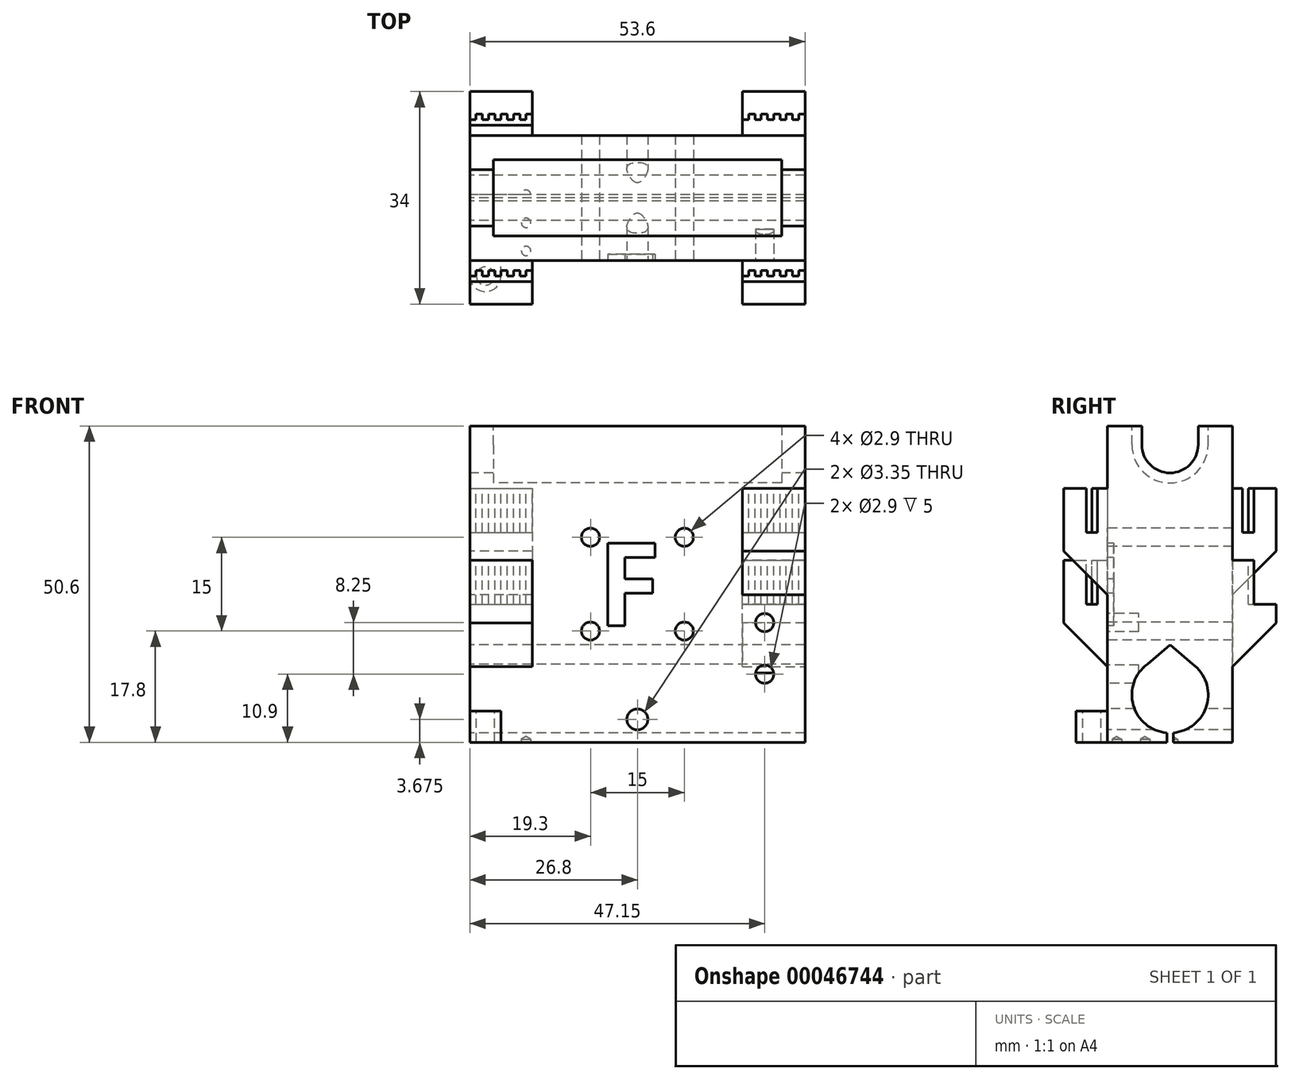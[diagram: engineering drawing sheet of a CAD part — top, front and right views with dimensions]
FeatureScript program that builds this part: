
annotation { "Feature Type Name" : "Feature", "Feature Type Description" : "" }
export const myFeature = defineFeature(function(context is Context, id is Id, definition is map)
    precondition{}
    {
        {
            assignVariable(context, id + "F0", {"name" : "LM8LUU", "anyValue" : 1.8});
        }
        {
            var Q0;
            Q0=qCreatedBy(makeId("Top.planeOp"),FACE);
            var sketch = newSketch(context, id + "F1", { "sketchPlane" : qUnion([Q0])});
            skLineSegment(sketch, "E0.bottom", {"start": v(0, 0) * mm, "end": v(53.6, 0) * mm});
            skLineSegment(sketch, "E0.top", {"start": v(0, 20) * mm, "end": v(53.6, 20) * mm});
            skLineSegment(sketch, "E0.left", {"start": v(0, 0) * mm, "end": v(0, 20) * mm});
            skLineSegment(sketch, "E0.right", {"start": v(53.6, 0) * mm, "end": v(53.6, 20) * mm});
            skSolve(sketch);
        }
        {
            var Q0;
            Q0=qSketchRegion(id+"F1",true);
            extrude(context, id + "F2", {"entities" : qUnion([Q0]), "depth" : 50.6 * mm});
        }
        {
            var Q0;
            Q0=makeQuery(id+"F2.opExtrude","SWEPT_FACE",FACE,{"disambiguationData":[OSD([sQuery(id+"F1.wireOp",EDGE,"E0.left")])]});
            var sketch = newSketch(context, id + "F3", { "sketchPlane" : qUnion([Q0])});
            skCircle(sketch, "E1", {"center": v(-10, 7.6) * mm, "radius": 6.1 * mm});
            skCircle(sketch, "E2", {"center": v(-10, 47.6) * mm, "radius": 4.5 * mm});
            skLineSegment(sketch, "E3", {"start": v(-20, 47.6) * mm, "end": v(0, 47.6) * mm, "construction": true});
            skLineSegment(sketch, "E4", {"start": v(-14.5, 50.6) * mm, "end": v(-14.5, 47.6) * mm});
            skLineSegment(sketch, "E5", {"start": v(-5.5, 50.6) * mm, "end": v(-5.5, 47.6) * mm});
            skLineSegment(sketch, "E6", {"start": v(-20, 7.6) * mm, "end": v(0, 7.6) * mm, "construction": true});
            skLineSegment(sketch, "E7", {"start": v(-10, 7.6) * mm, "end": v(-10, 0) * mm, "construction": true});
            skLineSegment(sketch, "E8", {"start": v(-10, 0) * mm, "end": v(-10.5, 0) * mm});
            skLineSegment(sketch, "E9", {"start": v(-10.5, 0) * mm, "end": v(-10.5, 1.52) * mm});
            skLineSegment(sketch, "E10", {"start": v(-10.5, 1.52) * mm, "end": v(-9.5, 1.52) * mm});
            skLineSegment(sketch, "E11", {"start": v(-9.5, 1.52) * mm, "end": v(-9.5, 0) * mm});
            skLineSegment(sketch, "E12", {"start": v(-9.5, 0) * mm, "end": v(-10, 0) * mm});
            skLineSegment(sketch, "E13", {"start": v(-10, 13.7) * mm, "end": v(-10, 15.6) * mm});
            skLineSegment(sketch, "E14", {"start": v(-10, 15.6) * mm, "end": v(-6.39, 12.51) * mm});
            skLineSegment(sketch, "E15", {"start": v(-10, 15.6) * mm, "end": v(-13.61, 12.51) * mm});
            skCircle(sketch, "E16", {"center": v(-10, 47.6) * mm, "radius": 6.1 * mm});
            skLineSegment(sketch, "E17", {"start": v(-3.9, 47.6) * mm, "end": v(-3.9, 50.6) * mm});
            skLineSegment(sketch, "E18", {"start": v(-16.1, 47.6) * mm, "end": v(-16.1, 50.6) * mm});
            skSolve(sketch);
        }
        {
            var Q0;
            {var subQ0=sQuery(id+"F3.wireOp",EDGE,"E14");var subQ1=sQuery(id+"F3.wireOp",EDGE,"E1");var subQ3=makeQuery(id+"F3.imprint","INTERSECT",VERTEX,{"disambiguationData":[OD(0.0)],"derivedFrom":[subQ1,subQ0]});Q0=makeQuery(id+"F3.imprint","IMPRINT",FACE,{"disambiguationData":[TD([[makeQuery(id+"F3.imprint","IMPRINT",EDGE,{"disambiguationData":[TD([[subQ3,-1.0]])],"derivedFrom":subQ1}),1.0]])]});}
            var Q1;
            {var subQ0=sQuery(id+"F3.wireOp",EDGE,"E15");var subQ1=sQuery(id+"F3.wireOp",EDGE,"E1");var subQ3=makeQuery(id+"F3.imprint","INTERSECT",VERTEX,{"disambiguationData":[OD(0.0)],"derivedFrom":[subQ1,subQ0]});Q1=makeQuery(id+"F3.imprint","IMPRINT",FACE,{"disambiguationData":[TD([[makeQuery(id+"F3.imprint","IMPRINT",EDGE,{"disambiguationData":[TD([[subQ3,1.0]])],"derivedFrom":subQ1}),1.0]])]});}
            var Q2;
            Q2=makeQuery(id+"F3.imprint","IMPRINT",FACE,{"disambiguationData":[TD([[makeQuery(id+"F3.imprint","IMPRINT",EDGE,{"derivedFrom":sQuery(id+"F3.wireOp",EDGE,"E8")}),-1.0]])]});
            var Q3;
            {var subQ0=sQuery(id+"F3.wireOp",EDGE,"E10");Q3=makeQuery(id+"F3.imprint","IMPRINT",FACE,{"disambiguationData":[TD([[makeQuery(id+"F3.imprint","IMPRINT",EDGE,{"derivedFrom":subQ0}),-1.0]])]});}
            var Q4;
            {var subQ3=sQuery(id+"F3.wireOp",EDGE,"E13");Q4=makeQuery(id+"F3.imprint","IMPRINT",FACE,{"disambiguationData":[TD([[makeQuery(id+"F3.imprint","IMPRINT",EDGE,{"derivedFrom":subQ3}),-1.0]])]});}
            var Q5;
            {var subQ3=sQuery(id+"F3.wireOp",EDGE,"E13");Q5=makeQuery(id+"F3.imprint","IMPRINT",FACE,{"disambiguationData":[TD([[makeQuery(id+"F3.imprint","IMPRINT",EDGE,{"derivedFrom":subQ3}),1.0]])]});}
            var Q6;
            {var subQ7=sQuery(id+"F3.wireOp",EDGE,"E10");Q6=makeQuery(id+"F3.imprint","IMPRINT",FACE,{"disambiguationData":[TD([[makeQuery(id+"F3.imprint","IMPRINT",EDGE,{"derivedFrom":subQ7}),1.0]])]});}
            var Q7;
            {var subQ3=sQuery(id+"F3.wireOp",EDGE,"E5");Q7=makeQuery(id+"F3.imprint","IMPRINT",FACE,{"disambiguationData":[TD([[makeQuery(id+"F3.imprint","IMPRINT",EDGE,{"derivedFrom":subQ3}),-1.0]])]});}
            var Q8;
            {var subQ0=sQuery(id+"F3.wireOp",EDGE,"E4");Q8=makeQuery(id+"F3.imprint","IMPRINT",FACE,{"disambiguationData":[TD([[makeQuery(id+"F3.imprint","IMPRINT",EDGE,{"derivedFrom":subQ0}),1.0]])]});}
            var Q9;
            {var subQ0=sQuery(id+"F3.wireOp",EDGE,"E4");Q9=makeQuery(id+"F3.imprint","IMPRINT",FACE,{"disambiguationData":[TD([[makeQuery(id+"F3.imprint","IMPRINT",EDGE,{"derivedFrom":subQ0}),1.0]])]});}
            var Q10;
            {var subQ3=sQuery(id+"F3.wireOp",EDGE,"E5");Q10=makeQuery(id+"F3.imprint","IMPRINT",FACE,{"disambiguationData":[TD([[makeQuery(id+"F3.imprint","IMPRINT",EDGE,{"derivedFrom":subQ3}),-1.0]])]});}
            var Q11;
            {var subQ1=sQuery(id+"F3.wireOp",EDGE,"E2");var subQ4=makeQuery(id+"F3.imprint","INTERSECT",VERTEX,{"derivedFrom":[subQ1,sQuery(id+"F3.wireOp",EDGE,"E5")]});Q11=makeQuery(id+"F3.imprint","IMPRINT",FACE,{"disambiguationData":[TD([[makeQuery(id+"F3.imprint","IMPRINT",EDGE,{"disambiguationData":[TD([[subQ4,-1.0]])],"derivedFrom":subQ1}),1.0]])]});}
            extrude(context, id + "F4", {"entities" : qUnion([Q0, Q1, Q2, Q3, Q4, Q5, Q6, Q7, Q8, Q9, Q10, Q11]), "operationType" : NewBodyOperationType.REMOVE, "endBound" : BoundingType.THROUGH_ALL, "oppositeDirection" : true, "depth" : 25 * mm});
        }
        {
            var Q0;
            {var subQ3=sQuery(id+"F3.wireOp",EDGE,"E4");Q0=makeQuery(id+"F3.imprint","IMPRINT",FACE,{"disambiguationData":[TD([[makeQuery(id+"F3.imprint","IMPRINT",EDGE,{"derivedFrom":subQ3}),-1.0]])]});}
            var Q1;
            {var subQ3=sQuery(id+"F3.wireOp",EDGE,"E18");Q1=makeQuery(id+"F3.imprint","IMPRINT",FACE,{"disambiguationData":[TD([[makeQuery(id+"F3.imprint","IMPRINT",EDGE,{"derivedFrom":subQ3}),-1.0]])]});}
            var Q2;
            {var subQ3=sQuery(id+"F3.wireOp",EDGE,"E17");Q2=makeQuery(id+"F3.imprint","IMPRINT",FACE,{"disambiguationData":[TD([[makeQuery(id+"F3.imprint","IMPRINT",EDGE,{"derivedFrom":subQ3}),1.0]])]});}
            extrude(context, id + "F5", {"entities" : qUnion([Q0, Q1, Q2]), "operationType" : NewBodyOperationType.REMOVE, "oppositeDirection" : true, "depth" : (46.25 + getVariable(context, 'LM8LUU') * 2) * mm});
        }
        {
            var Q0;
            {var subQ3=sQuery(id+"F3.wireOp",EDGE,"E4");Q0=makeQuery(id+"F3.imprint","IMPRINT",FACE,{"disambiguationData":[TD([[makeQuery(id+"F3.imprint","IMPRINT",EDGE,{"derivedFrom":subQ3}),-1.0]])]});}
            var Q1;
            {var subQ3=sQuery(id+"F3.wireOp",EDGE,"E18");Q1=makeQuery(id+"F3.imprint","IMPRINT",FACE,{"disambiguationData":[TD([[makeQuery(id+"F3.imprint","IMPRINT",EDGE,{"derivedFrom":subQ3}),-1.0]])]});}
            var Q2;
            {var subQ3=sQuery(id+"F3.wireOp",EDGE,"E17");Q2=makeQuery(id+"F3.imprint","IMPRINT",FACE,{"disambiguationData":[TD([[makeQuery(id+"F3.imprint","IMPRINT",EDGE,{"derivedFrom":subQ3}),1.0]])]});}
            extrude(context, id + "F6", {"entities" : qUnion([Q0, Q1, Q2]), "operationType" : NewBodyOperationType.ADD, "oppositeDirection" : true, "depth" : (26.75 - getVariable(context, 'LM8LUU')) * mm});
        }
        {
            var Q0;
            {var subQ3=sQuery(id+"F3.wireOp",EDGE,"E4");Q0=makeQuery(id+"F3.imprint","IMPRINT",FACE,{"disambiguationData":[TD([[makeQuery(id+"F3.imprint","IMPRINT",EDGE,{"derivedFrom":subQ3}),-1.0]])]});}
            var Q1;
            {var subQ3=sQuery(id+"F3.wireOp",EDGE,"E18");Q1=makeQuery(id+"F3.imprint","IMPRINT",FACE,{"disambiguationData":[TD([[makeQuery(id+"F3.imprint","IMPRINT",EDGE,{"derivedFrom":subQ3}),-1.0]])]});}
            var Q2;
            {var subQ3=sQuery(id+"F3.wireOp",EDGE,"E17");Q2=makeQuery(id+"F3.imprint","IMPRINT",FACE,{"disambiguationData":[TD([[makeQuery(id+"F3.imprint","IMPRINT",EDGE,{"derivedFrom":subQ3}),1.0]])]});}
            extrude(context, id + "F7", {"entities" : qUnion([Q0, Q1, Q2]), "operationType" : NewBodyOperationType.REMOVE, "oppositeDirection" : true, "depth" : (23.25 + getVariable(context, 'LM8LUU')) * mm});
        }
        {
            var Q0;
            {var subQ3=sQuery(id+"F3.wireOp",EDGE,"E4");Q0=makeQuery(id+"F3.imprint","IMPRINT",FACE,{"disambiguationData":[TD([[makeQuery(id+"F3.imprint","IMPRINT",EDGE,{"derivedFrom":subQ3}),-1.0]])]});}
            var Q1;
            {var subQ3=sQuery(id+"F3.wireOp",EDGE,"E18");Q1=makeQuery(id+"F3.imprint","IMPRINT",FACE,{"disambiguationData":[TD([[makeQuery(id+"F3.imprint","IMPRINT",EDGE,{"derivedFrom":subQ3}),-1.0]])]});}
            var Q2;
            {var subQ3=sQuery(id+"F3.wireOp",EDGE,"E17");Q2=makeQuery(id+"F3.imprint","IMPRINT",FACE,{"disambiguationData":[TD([[makeQuery(id+"F3.imprint","IMPRINT",EDGE,{"derivedFrom":subQ3}),1.0]])]});}
            extrude(context, id + "F8", {"entities" : qUnion([Q0, Q1, Q2]), "operationType" : NewBodyOperationType.ADD, "oppositeDirection" : true, "depth" : 3.75 * mm});
        }
        {
            var Q0;
            Q0=makeQuery(id+"F2.opExtrude","SWEPT_FACE",FACE,{"disambiguationData":[OSD([sQuery(id+"F1.wireOp",EDGE,"E0.bottom")])]});
            var sketch = newSketch(context, id + "F9", { "sketchPlane" : qUnion([Q0])});
            skLineSegment(sketch, "E19.bottom", {"start": v(0, 29.1) * mm, "end": v(10, 29.1) * mm});
            skLineSegment(sketch, "E19.top", {"start": v(0, 9.1) * mm, "end": v(10, 9.1) * mm});
            skLineSegment(sketch, "E19.left", {"start": v(0, 29.1) * mm, "end": v(0, 9.1) * mm});
            skLineSegment(sketch, "E19.right", {"start": v(10, 29.1) * mm, "end": v(10, 9.1) * mm});
            skLineSegment(sketch, "E20.bottom", {"start": v(53.6, 40.6) * mm, "end": v(43.6, 40.6) * mm});
            skLineSegment(sketch, "E20.top", {"start": v(53.6, 20.6) * mm, "end": v(43.6, 20.6) * mm});
            skLineSegment(sketch, "E20.left", {"start": v(53.6, 40.6) * mm, "end": v(53.6, 20.6) * mm});
            skLineSegment(sketch, "E20.right", {"start": v(43.6, 40.6) * mm, "end": v(43.6, 20.6) * mm});
            skPoint(sketch, "E21", {"position": v(0, 47.6) * mm});
            skPoint(sketch, "E22", {"position": v(0, 8.6) * mm});
            skSolve(sketch);
        }
        {
            var Q0;
            Q0=qSketchRegion(id+"F9",true);
            extrude(context, id + "F10", {"entities" : qUnion([Q0]), "operationType" : NewBodyOperationType.ADD, "depth" : 7 * mm});
        }
        {
            var Q0;
            Q0=makeQuery(id+"F10.opExtrude","CAP_EDGE",EDGE,{"disambiguationData":[OSD([sQuery(id+"F9.wireOp",EDGE,"E19.top")])],"isStart":false});
            var Q1;
            Q1=makeQuery(id+"F10.opExtrude","CAP_EDGE",EDGE,{"disambiguationData":[OSD([sQuery(id+"F9.wireOp",EDGE,"E20.top")])],"isStart":false});
            chamfer(context, id + "F11", {"entities" : qUnion([Q0, Q1]), "width" : 10 * mm, "tangentPropagation" : true});
        }
        {
            var Q0;
            Q0=makeQuery(id+"F10.opExtrude","SWEPT_FACE",FACE,{"disambiguationData":[OSD([sQuery(id+"F9.wireOp",EDGE,"E19.bottom")])]});
            var sketch = newSketch(context, id + "F12", { "sketchPlane" : qUnion([Q0])});
            skLineSegment(sketch, "E23", {"start": v(-935.9, 0) * mm, "end": v(-935.88, -4.54) * mm});
            skLineSegment(sketch, "E24.left", {"start": v(0, -3.4) * mm, "end": v(0, -1.6) * mm});
            skLineSegment(sketch, "E25", {"start": v(6, -2.5) * mm, "end": v(7, -2.5) * mm});
            skLineSegment(sketch, "E26", {"start": v(4, -2.5) * mm, "end": v(5, -2.5) * mm});
            skLineSegment(sketch, "E27", {"start": v(0, -2.5) * mm, "end": v(1, -2.5) * mm});
            skLineSegment(sketch, "E28", {"start": v(7, -1.6) * mm, "end": v(8, -1.6) * mm});
            skLineSegment(sketch, "E29", {"start": v(2, -2.5) * mm, "end": v(3, -2.5) * mm});
            skLineSegment(sketch, "E30", {"start": v(3, -1.6) * mm, "end": v(4, -1.6) * mm});
            skLineSegment(sketch, "E31", {"start": v(8, -2.5) * mm, "end": v(9, -2.5) * mm});
            skLineSegment(sketch, "E32", {"start": v(8, -1.6) * mm, "end": v(8, -2.5) * mm});
            skLineSegment(sketch, "E33", {"start": v(9, -2.5) * mm, "end": v(9, -1.6) * mm});
            skLineSegment(sketch, "E34", {"start": v(10, -1.6) * mm, "end": v(10, -2.5) * mm});
            skLineSegment(sketch, "E35", {"start": v(6, -1.6) * mm, "end": v(6, -2.5) * mm});
            skLineSegment(sketch, "E36", {"start": v(2, -1.6) * mm, "end": v(2, -2.5) * mm});
            skLineSegment(sketch, "E37", {"start": v(1, -1.6) * mm, "end": v(2, -1.6) * mm});
            skLineSegment(sketch, "E38", {"start": v(1, -2.5) * mm, "end": v(1, -1.6) * mm});
            skLineSegment(sketch, "E39", {"start": v(9, -1.6) * mm, "end": v(10, -1.6) * mm});
            skLineSegment(sketch, "E40", {"start": v(5, -1.6) * mm, "end": v(6, -1.6) * mm});
            skLineSegment(sketch, "E41", {"start": v(5, -2.5) * mm, "end": v(5, -1.6) * mm});
            skLineSegment(sketch, "E42", {"start": v(3, -2.5) * mm, "end": v(3, -1.6) * mm});
            skLineSegment(sketch, "E43", {"start": v(4, -1.6) * mm, "end": v(4, -2.5) * mm});
            skLineSegment(sketch, "E44", {"start": v(7, -2.5) * mm, "end": v(7, -1.6) * mm});
            skLineSegment(sketch, "E45", {"start": v(0, -1.6) * mm, "end": v(0, -2.5) * mm});
            skLineSegment(sketch, "E46", {"start": v(10, -2.5) * mm, "end": v(10, -3.4) * mm});
            skLineSegment(sketch, "E47", {"start": v(0, -3.4) * mm, "end": v(10, -3.4) * mm});
            skLineSegment(sketch, "E48", {"start": v(5.3, -1.6) * mm, "end": v(5.3, 0) * mm});
            skSolve(sketch);
        }
        {
            var Q0;
            Q0=qSketchRegion(id+"F12",true);
            extrude(context, id + "F13", {"entities" : qUnion([Q0]), "operationType" : NewBodyOperationType.REMOVE, "oppositeDirection" : true, "depth" : 7 * mm});
        }
        {
            var Q0;
            Q0=makeQuery(id+"F10.opExtrude","SWEPT_FACE",FACE,{"disambiguationData":[OSD([sQuery(id+"F9.wireOp",EDGE,"E20.bottom")])]});
            var sketch = newSketch(context, id + "F14", { "sketchPlane" : qUnion([Q0])});
            skLineSegment(sketch, "E49.left", {"start": v(43.6, -3.4) * mm, "end": v(43.6, -1.6) * mm});
            skLineSegment(sketch, "E50", {"start": v(49.6, -2.5) * mm, "end": v(50.6, -2.5) * mm});
            skLineSegment(sketch, "E51", {"start": v(47.6, -2.5) * mm, "end": v(48.6, -2.5) * mm});
            skLineSegment(sketch, "E52", {"start": v(43.6, -2.5) * mm, "end": v(44.6, -2.5) * mm});
            skLineSegment(sketch, "E53", {"start": v(50.6, -1.6) * mm, "end": v(51.6, -1.6) * mm});
            skLineSegment(sketch, "E54", {"start": v(45.6, -2.5) * mm, "end": v(46.6, -2.5) * mm});
            skLineSegment(sketch, "E55", {"start": v(46.6, -1.6) * mm, "end": v(47.6, -1.6) * mm});
            skLineSegment(sketch, "E56", {"start": v(51.6, -2.5) * mm, "end": v(52.6, -2.5) * mm});
            skLineSegment(sketch, "E57", {"start": v(51.6, -1.6) * mm, "end": v(51.6, -2.5) * mm});
            skLineSegment(sketch, "E58", {"start": v(52.6, -2.5) * mm, "end": v(52.6, -1.6) * mm});
            skLineSegment(sketch, "E59", {"start": v(53.6, -1.6) * mm, "end": v(53.6, -2.5) * mm});
            skLineSegment(sketch, "E60", {"start": v(49.6, -1.6) * mm, "end": v(49.6, -2.5) * mm});
            skLineSegment(sketch, "E61", {"start": v(45.6, -1.6) * mm, "end": v(45.6, -2.5) * mm});
            skLineSegment(sketch, "E62", {"start": v(44.6, -1.6) * mm, "end": v(45.6, -1.6) * mm});
            skLineSegment(sketch, "E63", {"start": v(44.6, -2.5) * mm, "end": v(44.6, -1.6) * mm});
            skLineSegment(sketch, "E64", {"start": v(52.6, -1.6) * mm, "end": v(53.6, -1.6) * mm});
            skLineSegment(sketch, "E65", {"start": v(48.6, -1.6) * mm, "end": v(49.6, -1.6) * mm});
            skLineSegment(sketch, "E66", {"start": v(48.6, -2.5) * mm, "end": v(48.6, -1.6) * mm});
            skLineSegment(sketch, "E67", {"start": v(46.6, -2.5) * mm, "end": v(46.6, -1.6) * mm});
            skLineSegment(sketch, "E68", {"start": v(47.6, -1.6) * mm, "end": v(47.6, -2.5) * mm});
            skLineSegment(sketch, "E69", {"start": v(50.6, -2.5) * mm, "end": v(50.6, -1.6) * mm});
            skLineSegment(sketch, "E70", {"start": v(43.6, -1.6) * mm, "end": v(43.6, -2.5) * mm});
            skLineSegment(sketch, "E71", {"start": v(53.6, -2.5) * mm, "end": v(53.6, -3.4) * mm});
            skLineSegment(sketch, "E72", {"start": v(43.6, -3.4) * mm, "end": v(53.6, -3.4) * mm});
            skLineSegment(sketch, "E73", {"start": v(48.83, -1.6) * mm, "end": v(48.83, 0) * mm});
            skSolve(sketch);
        }
        {
            var Q0;
            Q0=qSketchRegion(id+"F14",true);
            extrude(context, id + "F15", {"entities" : qUnion([Q0]), "operationType" : NewBodyOperationType.REMOVE, "oppositeDirection" : true, "depth" : 7 * mm});
        }
        {
            var Q0;
            Q0=makeQuery(id+"F2.opExtrude","SWEPT_FACE",FACE,{"disambiguationData":[OSD([sQuery(id+"F1.wireOp",EDGE,"E0.top")])]});
            var sketch = newSketch(context, id + "F16", { "sketchPlane" : qUnion([Q0])});
            skLineSegment(sketch, "E74.bottom", {"start": v(-53.6, 9.1) * mm, "end": v(-43.6, 9.1) * mm});
            skLineSegment(sketch, "E74.top", {"start": v(-53.6, 29.1) * mm, "end": v(-43.6, 29.1) * mm});
            skLineSegment(sketch, "E74.left", {"start": v(-53.6, 9.1) * mm, "end": v(-53.6, 29.1) * mm});
            skLineSegment(sketch, "E74.right", {"start": v(-43.6, 9.1) * mm, "end": v(-43.6, 29.1) * mm});
            skLineSegment(sketch, "E75.bottom", {"start": v(0, 40.6) * mm, "end": v(-10, 40.6) * mm});
            skLineSegment(sketch, "E75.top", {"start": v(0, 20.6) * mm, "end": v(-10, 20.6) * mm});
            skLineSegment(sketch, "E75.left", {"start": v(0, 40.6) * mm, "end": v(0, 20.6) * mm});
            skLineSegment(sketch, "E75.right", {"start": v(-10, 40.6) * mm, "end": v(-10, 20.6) * mm});
            skSolve(sketch);
        }
        {
            var Q0;
            Q0=qSketchRegion(id+"F16",true);
            extrude(context, id + "F17", {"entities" : qUnion([Q0]), "operationType" : NewBodyOperationType.ADD, "depth" : 7 * mm});
        }
        {
            var Q0;
            Q0=makeQuery(id+"F17.opExtrude","SWEPT_FACE",FACE,{"disambiguationData":[OSD([sQuery(id+"F16.wireOp",EDGE,"E74.top")])]});
            var sketch = newSketch(context, id + "F18", { "sketchPlane" : qUnion([Q0])});
            skLineSegment(sketch, "E76.left", {"start": v(43.6, 21.6) * mm, "end": v(43.6, 23.4) * mm});
            skLineSegment(sketch, "E77", {"start": v(49.6, 22.5) * mm, "end": v(50.6, 22.5) * mm});
            skLineSegment(sketch, "E78", {"start": v(47.6, 22.5) * mm, "end": v(48.6, 22.5) * mm});
            skLineSegment(sketch, "E79", {"start": v(43.6, 22.5) * mm, "end": v(44.6, 22.5) * mm});
            skLineSegment(sketch, "E80", {"start": v(50.6, 23.4) * mm, "end": v(51.6, 23.4) * mm});
            skLineSegment(sketch, "E81", {"start": v(45.6, 22.5) * mm, "end": v(46.6, 22.5) * mm});
            skLineSegment(sketch, "E82", {"start": v(46.6, 23.4) * mm, "end": v(47.6, 23.4) * mm});
            skLineSegment(sketch, "E83", {"start": v(51.6, 22.5) * mm, "end": v(52.6, 22.5) * mm});
            skLineSegment(sketch, "E84", {"start": v(51.6, 23.4) * mm, "end": v(51.6, 22.5) * mm});
            skLineSegment(sketch, "E85", {"start": v(52.6, 22.5) * mm, "end": v(52.6, 23.4) * mm});
            skLineSegment(sketch, "E86", {"start": v(53.6, 23.4) * mm, "end": v(53.6, 22.5) * mm});
            skLineSegment(sketch, "E87", {"start": v(49.6, 23.4) * mm, "end": v(49.6, 22.5) * mm});
            skLineSegment(sketch, "E88", {"start": v(45.6, 23.4) * mm, "end": v(45.6, 22.5) * mm});
            skLineSegment(sketch, "E89", {"start": v(44.6, 23.4) * mm, "end": v(45.6, 23.4) * mm});
            skLineSegment(sketch, "E90", {"start": v(44.6, 22.5) * mm, "end": v(44.6, 23.4) * mm});
            skLineSegment(sketch, "E91", {"start": v(52.6, 23.4) * mm, "end": v(53.6, 23.4) * mm});
            skLineSegment(sketch, "E92", {"start": v(48.6, 23.4) * mm, "end": v(49.6, 23.4) * mm});
            skLineSegment(sketch, "E93", {"start": v(48.6, 22.5) * mm, "end": v(48.6, 23.4) * mm});
            skLineSegment(sketch, "E94", {"start": v(46.6, 22.5) * mm, "end": v(46.6, 23.4) * mm});
            skLineSegment(sketch, "E95", {"start": v(47.6, 23.4) * mm, "end": v(47.6, 22.5) * mm});
            skLineSegment(sketch, "E96", {"start": v(50.6, 22.5) * mm, "end": v(50.6, 23.4) * mm});
            skLineSegment(sketch, "E97", {"start": v(43.6, 23.4) * mm, "end": v(43.6, 22.5) * mm});
            skLineSegment(sketch, "E98", {"start": v(53.6, 22.5) * mm, "end": v(53.6, 21.6) * mm});
            skLineSegment(sketch, "E99", {"start": v(43.6, 21.6) * mm, "end": v(53.6, 21.6) * mm});
            skLineSegment(sketch, "E100", {"start": v(48.6, 21.6) * mm, "end": v(48.6, 20) * mm});
            skSolve(sketch);
        }
        {
            var Q0;
            {var subQ4=sQuery(id+"F18.wireOp",EDGE,"E76.left");Q0=makeQuery(id+"F18.imprint","IMPRINT",FACE,{"disambiguationData":[TD([[makeQuery(id+"F18.imprint","IMPRINT",EDGE,{"derivedFrom":subQ4}),1.0]])]});}
            extrude(context, id + "F19", {"entities" : qUnion([Q0]), "operationType" : NewBodyOperationType.REMOVE, "oppositeDirection" : true, "depth" : 7 * mm});
        }
        {
            var Q0;
            Q0=makeQuery(id+"F17.opExtrude","SWEPT_FACE",FACE,{"disambiguationData":[OSD([sQuery(id+"F16.wireOp",EDGE,"E75.bottom")])]});
            var sketch = newSketch(context, id + "F20", { "sketchPlane" : qUnion([Q0])});
            skLineSegment(sketch, "E101", {"start": v(6, 22.5) * mm, "end": v(7, 22.5) * mm});
            skLineSegment(sketch, "E102", {"start": v(4, 22.5) * mm, "end": v(5, 22.5) * mm});
            skLineSegment(sketch, "E103", {"start": v(0, 22.5) * mm, "end": v(1, 22.5) * mm});
            skLineSegment(sketch, "E104", {"start": v(7, 23.4) * mm, "end": v(8, 23.4) * mm});
            skLineSegment(sketch, "E105", {"start": v(2, 22.5) * mm, "end": v(3, 22.5) * mm});
            skLineSegment(sketch, "E106", {"start": v(3, 23.4) * mm, "end": v(4, 23.4) * mm});
            skLineSegment(sketch, "E107", {"start": v(8, 22.5) * mm, "end": v(9, 22.5) * mm});
            skLineSegment(sketch, "E108", {"start": v(8, 23.4) * mm, "end": v(8, 22.5) * mm});
            skLineSegment(sketch, "E109", {"start": v(9, 22.5) * mm, "end": v(9, 23.4) * mm});
            skLineSegment(sketch, "E110", {"start": v(10, 23.4) * mm, "end": v(10, 22.5) * mm});
            skLineSegment(sketch, "E111", {"start": v(6, 23.4) * mm, "end": v(6, 22.5) * mm});
            skLineSegment(sketch, "E112", {"start": v(2, 23.4) * mm, "end": v(2, 22.5) * mm});
            skLineSegment(sketch, "E113", {"start": v(1, 23.4) * mm, "end": v(2, 23.4) * mm});
            skLineSegment(sketch, "E114", {"start": v(1, 22.5) * mm, "end": v(1, 23.4) * mm});
            skLineSegment(sketch, "E115", {"start": v(9, 23.4) * mm, "end": v(10, 23.4) * mm});
            skLineSegment(sketch, "E116", {"start": v(5, 23.4) * mm, "end": v(6, 23.4) * mm});
            skLineSegment(sketch, "E117", {"start": v(5, 22.5) * mm, "end": v(5, 23.4) * mm});
            skLineSegment(sketch, "E118", {"start": v(3, 22.5) * mm, "end": v(3, 23.4) * mm});
            skLineSegment(sketch, "E119", {"start": v(4, 23.4) * mm, "end": v(4, 22.5) * mm});
            skLineSegment(sketch, "E120", {"start": v(7, 22.5) * mm, "end": v(7, 23.4) * mm});
            skLineSegment(sketch, "E121", {"start": v(10, 22.5) * mm, "end": v(10, 21.6) * mm});
            skLineSegment(sketch, "E122", {"start": v(0, 21.6) * mm, "end": v(10, 21.6) * mm});
            skLineSegment(sketch, "E123", {"start": v(5, 21.6) * mm, "end": v(5, 20) * mm});
            skLineSegment(sketch, "E124", {"start": v(0, 21.6) * mm, "end": v(0, 22.5) * mm});
            skSolve(sketch);
        }
        {
            var Q0;
            Q0=makeQuery(id+"F20.imprint","IMPRINT",FACE,{"disambiguationData":[TD([[makeQuery(id+"F20.imprint","IMPRINT",EDGE,{"derivedFrom":sQuery(id+"F20.wireOp",EDGE,"E101")}),-1.0]])]});
            extrude(context, id + "F21", {"entities" : qUnion([Q0]), "operationType" : NewBodyOperationType.REMOVE, "oppositeDirection" : true, "depth" : 7 * mm});
        }
        {
            var Q0;
            Q0=makeQuery(id+"F17.opExtrude","CAP_EDGE",EDGE,{"disambiguationData":[OSD([sQuery(id+"F16.wireOp",EDGE,"E75.top")])],"isStart":false});
            var Q1;
            Q1=makeQuery(id+"F17.opExtrude","CAP_EDGE",EDGE,{"disambiguationData":[OSD([sQuery(id+"F16.wireOp",EDGE,"E74.bottom")])],"isStart":false});
            chamfer(context, id + "F22", {"entities" : qUnion([Q0, Q1]), "width" : 10 * mm, "tangentPropagation" : true});
        }
        {
            var Q0;
            Q0=makeQuery(id+"F2.opExtrude","SWEPT_FACE",FACE,{"disambiguationData":[OSD([sQuery(id+"F1.wireOp",EDGE,"E0.bottom")])]});
            var sketch = newSketch(context, id + "F23", { "sketchPlane" : qUnion([Q0])});
            skCircle(sketch, "E125", {"center": v(19.3, 32.8) * mm, "radius": 1.45 * mm});
            skCircle(sketch, "E126", {"center": v(34.3, 32.8) * mm, "radius": 1.45 * mm});
            skCircle(sketch, "E127", {"center": v(19.3, 17.8) * mm, "radius": 1.45 * mm});
            skCircle(sketch, "E128", {"center": v(34.3, 17.8) * mm, "radius": 1.45 * mm});
            skLineSegment(sketch, "E129", {"start": v(19.3, 32.8) * mm, "end": v(0, 32.8) * mm});
            skLineSegment(sketch, "E130", {"start": v(34.3, 17.8) * mm, "end": v(53.6, 17.8) * mm});
            skLineSegment(sketch, "E131", {"start": v(34.3, 32.8) * mm, "end": v(34.3, 50.6) * mm});
            skLineSegment(sketch, "E132", {"start": v(19.3, 17.8) * mm, "end": v(19.3, 0) * mm});
            skCircle(sketch, "E133", {"center": v(26.8, 3.68) * mm, "radius": 1.68 * mm});
            skLineSegment(sketch, "E134", {"start": v(26.8, 0) * mm, "end": v(26.8, 13.82) * mm, "construction": true});
            skSolve(sketch);
        }
        {
            var Q0;
            Q0=qSketchRegion(id+"F23",true);
            var Q1;
            Q1=makeQuery(id+"F23.imprint","IMPRINT",FACE,{"disambiguationData":[TD([[makeQuery(id+"F23.imprint","IMPRINT",EDGE,{"derivedFrom":sQuery(id+"F23.wireOp",EDGE,"E125")}),1.0]])]});
            var Q2;
            Q2=makeQuery(id+"F23.imprint","IMPRINT",FACE,{"disambiguationData":[TD([[makeQuery(id+"F23.imprint","IMPRINT",EDGE,{"derivedFrom":sQuery(id+"F23.wireOp",EDGE,"E126")}),1.0]])]});
            var Q3;
            Q3=makeQuery(id+"F23.imprint","IMPRINT",FACE,{"disambiguationData":[TD([[makeQuery(id+"F23.imprint","IMPRINT",EDGE,{"derivedFrom":sQuery(id+"F23.wireOp",EDGE,"E128")}),1.0]])]});
            var Q4;
            Q4=makeQuery(id+"F23.imprint","IMPRINT",FACE,{"disambiguationData":[TD([[makeQuery(id+"F23.imprint","IMPRINT",EDGE,{"derivedFrom":sQuery(id+"F23.wireOp",EDGE,"E127")}),1.0]])]});
            extrude(context, id + "F24", {"entities" : qUnion([Q0, Q1, Q2, Q3, Q4]), "operationType" : NewBodyOperationType.REMOVE, "endBound" : BoundingType.THROUGH_ALL, "oppositeDirection" : true, "depth" : 25 * mm});
        }
        {
            var Q0;
            Q0=makeQuery(id+"F2.opExtrude","SWEPT_FACE",FACE,{"disambiguationData":[OSD([sQuery(id+"F1.wireOp",EDGE,"E0.bottom")])]});
            var sketch = newSketch(context, id + "F25", { "sketchPlane" : qUnion([Q0])});
            skCircle(sketch, "E135", {"center": v(47.15, 19.15) * mm, "radius": 1.45 * mm});
            skCircle(sketch, "E136", {"center": v(47.15, 10.9) * mm, "radius": 1.45 * mm});
            skSolve(sketch);
        }
        {
            var Q0;
            Q0=qSketchRegion(id+"F25",true);
            extrude(context, id + "F26", {"entities" : qUnion([Q0]), "operationType" : NewBodyOperationType.REMOVE, "oppositeDirection" : true, "depth" : 5 * mm});
        }
        {
            var Q0;
            Q0=makeQuery(id+"F2.opExtrude","SWEPT_FACE",FACE,{"disambiguationData":[OSD([sQuery(id+"F1.wireOp",EDGE,"E0.bottom")])]});
            var sketch = newSketch(context, id + "F27", { "sketchPlane" : qUnion([Q0])});
            skText(sketch, "E137", { "text": "F", "fontName": "OpenSans-Bold.ttf"});
            skLineSegment(sketch, "E138", {"start": v(19.3, 32.8) * mm, "end": v(19.3, 17.8) * mm, "construction": true});
            skLineSegment(sketch, "E139", {"start": v(19.3, 17.8) * mm, "end": v(34.3, 17.8) * mm, "construction": true});
            skLineSegment(sketch, "E140", {"start": v(34.3, 17.8) * mm, "end": v(34.3, 32.8) * mm, "construction": true});
            skLineSegment(sketch, "E141", {"start": v(34.3, 32.8) * mm, "end": v(19.3, 32.8) * mm, "construction": true});
            skLineSegment(sketch, "E142", {"start": v(19.3, 25.3) * mm, "end": v(22.2, 25.3) * mm, "construction": true});
            skLineSegment(sketch, "E143", {"start": v(31.4, 25.3) * mm, "end": v(34.3, 25.3) * mm, "construction": true});
            skLineSegment(sketch, "E144", {"start": v(26.8, 18.66) * mm, "end": v(26.8, 17.8) * mm, "construction": true});
            skLineSegment(sketch, "E145", {"start": v(26.8, 32.8) * mm, "end": v(26.8, 31.94) * mm, "construction": true});
            const initialGuessF27  = {"E137": [0.0204, 0.01866, 1, 0, 0.01328]};
            skSetInitialGuess(sketch, initialGuessF27);
            skSolve(sketch);
        }
        {
            var Q0;
            Q0=qSketchRegion(id+"F27",true);
            extrude(context, id + "F28", {"entities" : qUnion([Q0]), "operationType" : NewBodyOperationType.REMOVE, "oppositeDirection" : true, "depth" : 1 * mm});
        }
        {
            var Q0;
            Q0=makeQuery(id+"F2.opExtrude","SWEPT_FACE",FACE,{"disambiguationData":[OSD([sQuery(id+"F1.wireOp",EDGE,"E0.bottom")])]});
            var sketch = newSketch(context, id + "F29", { "sketchPlane" : qUnion([Q0])});
            skLineSegment(sketch, "E146.bottom", {"start": v(0, 0) * mm, "end": v(5, 0) * mm});
            skLineSegment(sketch, "E146.top", {"start": v(0, 5) * mm, "end": v(5, 5) * mm});
            skLineSegment(sketch, "E146.left", {"start": v(0, 0) * mm, "end": v(0, 5) * mm});
            skLineSegment(sketch, "E146.right", {"start": v(5, 0) * mm, "end": v(5, 5) * mm});
            skSolve(sketch);
        }
        {
            var Q0;
            Q0=qSketchRegion(id+"F29",true);
            extrude(context, id + "F30", {"entities" : qUnion([Q0]), "operationType" : NewBodyOperationType.ADD, "depth" : 5 * mm});
        }
        {
            var Q0;
            Q0=makeQuery(id+"F30.opExtrude","SWEPT_FACE",FACE,{"disambiguationData":[OSD([sQuery(id+"F29.wireOp",EDGE,"E146.top")])]});
            var sketch = newSketch(context, id + "F31", { "sketchPlane" : qUnion([Q0])});
            skCircle(sketch, "E147", {"center": v(2.5, -2.5) * mm, "radius": 1.45 * mm});
            skLineSegment(sketch, "E148", {"start": v(0, -2.5) * mm, "end": v(5, -2.5) * mm});
            skSolve(sketch);
        }
        {
            var Q0;
            Q0=qSketchRegion(id+"F31",true);
            extrude(context, id + "F32", {"entities" : qUnion([Q0]), "operationType" : NewBodyOperationType.REMOVE, "oppositeDirection" : true, "depth" : 25 * mm});
        }
        {
            var Q0;
            Q0=makeQuery(id+"F30.opExtrude","CAP_EDGE",EDGE,{"disambiguationData":[OSD([sQuery(id+"F29.wireOp",EDGE,"E146.left")])],"isStart":false});
            var Q1;
            Q1=makeQuery(id+"F30.opExtrude","CAP_EDGE",EDGE,{"disambiguationData":[OSD([sQuery(id+"F29.wireOp",EDGE,"E146.right")])],"isStart":false});
            fillet(context, id + "F33", {"entities" : qUnion([Q0, Q1]), "radius" : 2.5 * mm, "tangentPropagation" : true, "allowEdgeOverflow" : false});
        }
        {
            var Q0;
            {var subQ0=sQuery(id+"F1.wireOp",EDGE,"E0.top");var subQ1=sQuery(id+"F1.wireOp",EDGE,"E0.left");var subQ2=sQuery(id+"F1.wireOp",EDGE,"E0.right");Q0=makeQuery(id+"F4.boolean.opBoolean","SPLIT",FACE,{"disambiguationData":[TD([makeQuery(id+"F2.opExtrude","SWEPT_FACE",FACE,{"disambiguationData":[OSD([subQ0])]})])],"derivedFrom":makeQuery(id+"F2.opExtrude","CAP_FACE",FACE,{"disambiguationData":[OSD([sQuery(id+"F1.wireOp",EDGE,"E0.bottom"),subQ0,subQ1,subQ2])],"isStart":true})});}
            var sketch = newSketch(context, id + "F34", { "sketchPlane" : qUnion([Q0])});
            skCircle(sketch, "E149", {"center": v(9, -1.5) * mm, "radius": 0.6 * mm});
            skCircle(sketch, "E150", {"center": v(9, -6) * mm, "radius": 0.6 * mm});
            skCircle(sketch, "E151", {"center": v(9, -10.5) * mm, "radius": 0.6 * mm});
            skCircle(sketch, "E152.0", {"center": v(2.5, 2.5) * mm, "radius": 1.45 * mm});
            skSolve(sketch);
        }
        {
            var Q0;
            Q0=sQuery(id+"F34.wireOp",VERTEX,"E150.center");
            var Q1;
            Q1=sQuery(id+"F34.wireOp",VERTEX,"E149.center");
            var Q2;
            Q2=sQuery(id+"F34.wireOp",VERTEX,"E151.center");
            var Q3;
            Q3=makeQuery(id+"F2.opExtrude","SWEPT_BODY",BODY,{"disambiguationData":[OSD([sQuery(id+"F1.wireOp",EDGE,"E0.bottom"),sQuery(id+"F1.wireOp",EDGE,"E0.top"),sQuery(id+"F1.wireOp",EDGE,"E0.left"),sQuery(id+"F1.wireOp",EDGE,"E0.right")])]});
            hole(context, id + "F35", {"style" : HoleStyle.SIMPLE, "holeDiameter" : 1.5 * mm, "endStyle" : HoleEndStyle.BLIND, "holeDepth" : 0.5 * mm, "locations" : qUnion([Q0, Q1, Q2]), "scope" : qUnion([Q3])});
        }
    });
